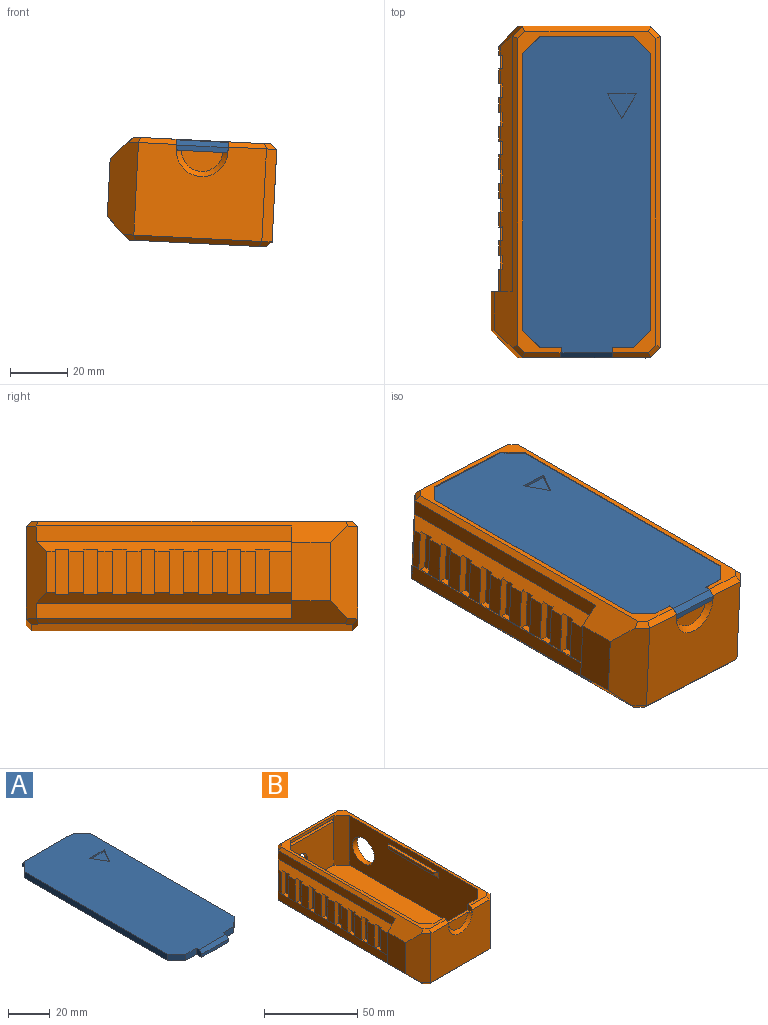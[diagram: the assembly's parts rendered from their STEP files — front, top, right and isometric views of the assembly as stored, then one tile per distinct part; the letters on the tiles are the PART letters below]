
ASSEMBLY  parts=2 mates=1
PART A: 24 faces, bbox 44.7x114.1x3.6 mm
  f0: plane 110.45x44.65mm, normal (0,0,1), area 4768.4mm2, adj f1,f2,f3,f4,f5,f7,f8,f9
  f1: plane 7.33x3.6mm, normal (0,-1,0), area 26.4mm2, adj f0,f6,f9,f16
  f2: plane 7.33x3.6mm, normal (0,-1,0), area 26.4mm2, adj f0,f6,f10,f17
  f3: plane 96.66x3.6mm, normal (1,0,0), area 348mm2, adj f0,f6,f7,f10
  f4: plane 32.65x1.8mm, normal (0,1,0), area 58.8mm2, adj f0,f7,f8,f11
  f5: plane 96.66x3.6mm, normal (-1,0,0), area 348mm2, adj f0,f6,f8,f9
  f6: plane 114.05x44.65mm, normal (0,0,-1), area 4902.9mm2, adj f1,f2,f3,f5,f7,f8,f9,f10
  f7: plane 6x6mm, normal (0.71,0.71,0), area 30.5mm2, adj f0,f3,f4,f6,f12
  f8: plane 6x6mm, normal (-0.71,0.71,0), area 30.5mm2, adj f0,f4,f5,f6,f13
  f9: plane 6x6mm, normal (-0.71,-0.71,0), area 30.5mm2, adj f0,f1,f5,f6
  f10: plane 6x6mm, normal (0.71,-0.71,0), area 30.5mm2, adj f0,f2,f3,f6
  f11: plane 32.65x1.55mm, normal (0,0,1), area 50.6mm2, adj f4,f12,f13,f15
  f12: plane 1.8x1.8mm, normal (1,0,0), area 3.2mm2, adj f6,f7,f11,f14,f15
  f13: plane 1.8x1.8mm, normal (-1,0,0), area 3.2mm2, adj f6,f8,f11,f14,f15
  f14: plane 32.65x1.55mm, normal (0,1,0), area 50.6mm2, adj f6,f12,f13,f15
  f15: cylinder r=0.25mm len=32.65mm, axis (-1,0,0), area 12.8mm2, adj f11,f12,f13,f14
  f16: plane 3.6x3.6mm, normal (-1,0,0), area 11.3mm2, adj f0,f1,f6,f18,f19
  f17: plane 3.6x3.6mm, normal (1,0,0), area 11.3mm2, adj f0,f2,f6,f18,f19
  f18: plane 18x1.8mm, normal (0,-1,0), area 32.4mm2, adj f6,f16,f17,f19
  f19: plane 18x1.8mm, normal (0,-0.71,0.71), area 45.8mm2, adj f0,f16,f17,f18
  f20: plane 8.66x5mm, normal (0.87,0.5,0), area 9mm2, adj f0,f21,f22,f23
  f21: plane 8.66x5mm, normal (-0.87,0.5,0), area 9mm2, adj f0,f20,f22,f23
  f22: plane 10x0.9mm, normal (0,-1,0), area 9mm2, adj f0,f20,f21,f23
  f23: plane 10x8.66mm, normal (0,0,1), area 43.3mm2, adj f20,f21,f22
PART B: 141 faces, bbox 58x116x36 mm
  f0: plane 14.4x3.01mm, normal (-1,0,0), area 43.4mm2, adj f21,f74,f75,f113
  f1: plane 14.4x5.23mm, normal (-1,0,0), area 75.3mm2, adj f74,f75,f109,f111
  f2: plane 14.4x5.23mm, normal (-1,0,0), area 75.3mm2, adj f74,f75,f104,f107
  f3: plane 14.4x5.23mm, normal (-1,0,0), area 75.3mm2, adj f74,f75,f99,f102
  f4: plane 14.4x5.23mm, normal (-1,0,0), area 75.3mm2, adj f74,f75,f94,f97
  f5: plane 14.4x5.23mm, normal (-1,0,0), area 75.3mm2, adj f74,f75,f89,f92
  f6: plane 14.4x5.23mm, normal (-1,0,0), area 75.3mm2, adj f74,f75,f84,f87
  f7: plane 14.4x5.23mm, normal (-1,0,0), area 75.3mm2, adj f74,f75,f79,f82
  f8: plane 89.2x5.4mm, normal (-1,0,0), area 481.7mm2, adj f21,f64,f72,f75
  f9: plane 89.2x5.4mm, normal (-1,0,0), area 481.7mm2, adj f21,f61,f72,f74
  f10: plane 96.81x32.4mm, normal (1,0,0), area 2998.7mm2, adj f14,f20,f26,f28,f44,f49,f50,f51
  f11: plane 96.81x32.4mm, normal (-1,0,0), area 2784.8mm2, adj f14,f20,f25,f27,f30,f42,f46,f47
  f12: plane 44.8x32.4mm, normal (0,1,0), area 999.1mm2, adj f21,f22,f39,f58,f66
  f13: plane 32.8x1.8mm, normal (0,-1,0), area 59mm2, adj f14,f27,f28,f37
  f14: plane 112.4x48.4mm, normal (0,0,1), area 592.5mm2, adj f10,f11,f13,f15,f25,f26,f27,f28
  f15: plane 32.8x32.4mm, normal (0,1,0), area 998.1mm2, adj f14,f20,f25,f26,f31,f32,f33
  f16: plane 44.8x32.4mm, normal (0,-1,0), area 1291.9mm2, adj f23,f24,f31,f33,f53,f57,f62,f70
  f17: plane 32.8x28.6mm, normal (0,-1,0), area 851.6mm2, adj f20,f27,f28,f29,f35
  f18: plane 108.8x32.4mm, normal (1,0,0), area 2646.8mm2, adj f22,f23,f30,f54,f68,f116,f117,f118
  f19: plane 112.4x48.4mm, normal (0,0,-1), area 5427.2mm2, adj f54,f55,f56,f57,f58,f59,f60,f61
  f20: plane 108.8x44.8mm, normal (0,0,1), area 4802.3mm2, adj f10,f11,f15,f17,f25,f26,f27,f28
  f21: plane 32.4x7.2mm, normal (-0.71,0.71,0), area 256.6mm2, adj f0,f8,f9,f12,f60,f65,f74,f75
  f22: plane 32.4x3.6mm, normal (0.71,0.71,0), area 165mm2, adj f12,f18,f56,f67
  f23: plane 32.4x3.6mm, normal (0.71,-0.71,0), area 165mm2, adj f16,f18,f55,f69
  f24: plane 32.4x9.6mm, normal (-0.71,-0.71,0), area 388.9mm2, adj f16,f59,f61,f63,f64,f73
  f25: plane 32.4x6mm, normal (-0.71,0.71,0), area 274.8mm2, adj f11,f14,f15,f20
  f26: plane 32.4x6mm, normal (0.71,0.71,0), area 274.8mm2, adj f10,f14,f15,f20
  f27: plane 32.4x6mm, normal (-0.71,-0.71,0), area 274.8mm2, adj f11,f13,f14,f17,f20,f36
  f28: plane 32.4x6mm, normal (0.71,-0.71,0), area 274.8mm2, adj f10,f13,f14,f17,f20,f34
  f29: cylinder r=5.25mm len=10.5mm, axis (0,1,0), area 85.8mm2, adj f17,f40
  f30: cylinder r=8.25mm len=16.5mm, axis (1,0,0), area 186.6mm2, adj f11,f18
  f31: plane 3.6x3.6mm, normal (1,0,0), area 11.3mm2, adj f14,f15,f16,f32,f62
  f32: plane 18x3.6mm, normal (0,0,1), area 35.6mm2, adj f15,f31,f33,f52,f53
  f33: plane 3.6x3.6mm, normal (-1,0,0), area 11.3mm2, adj f14,f15,f16,f32,f70
  f34: plane 2.1x2mm, normal (1,0,0), area 4.1mm2, adj f28,f35,f37,f38,f41
  f35: plane 32.8x2.1mm, normal (0,0,1), area 68.9mm2, adj f17,f34,f36,f38
  f36: plane 2.1x2mm, normal (-1,0,0), area 4.1mm2, adj f27,f35,f37,f38,f41
  f37: plane 32.8x1.6mm, normal (0,0,-1), area 52.5mm2, adj f13,f34,f36,f41
  f38: plane 32.8x1.5mm, normal (0,-1,0), area 49.2mm2, adj f34,f35,f36,f41
  f39: cylinder r=12mm len=24mm, axis (0,1,0), area 75.4mm2, adj f12,f40
  f40: plane 24x24mm, normal (0,1,0), area 365.8mm2, adj f29,f39
  f41: cylinder r=0.5mm len=32.8mm, axis (-1,0,0), area 25.8mm2, adj f34,f36,f37,f38
  f42: plane 38.28x1.8mm, normal (0,0,1), area 65.7mm2, adj f11,f43,f46,f48
  f43: plane 34.68x1.8mm, normal (-1,0,0), area 62.4mm2, adj f42,f46,f47,f48
  f44: plane 38.28x1.8mm, normal (0,0,1), area 65.7mm2, adj f10,f45,f49,f51
  f45: plane 34.68x1.8mm, normal (1,0,0), area 62.4mm2, adj f44,f49,f50,f51
  f46: plane 3.6x1.8mm, normal (-0.71,0.71,0), area 6.9mm2, adj f11,f42,f43,f47
  f47: plane 38.28x1.8mm, normal (-0.71,0,-0.71), area 92.9mm2, adj f11,f43,f46,f48
  f48: plane 3.6x1.8mm, normal (-0.71,-0.71,0), area 6.9mm2, adj f11,f42,f43,f47
  f49: plane 3.6x1.8mm, normal (0.71,-0.71,0), area 6.9mm2, adj f10,f44,f45,f50
  f50: plane 38.28x1.8mm, normal (0.71,0,-0.71), area 92.9mm2, adj f10,f45,f49,f51
  f51: plane 3.6x1.8mm, normal (0.71,0.71,0), area 6.9mm2, adj f10,f44,f45,f50
  f52: plane 14.4x7.2mm, normal (0,-1,0), area 81.4mm2, adj f32,f53
  f53: cone r=7.2mm half-angle=45deg, axis (0,-1,0), area 64.8mm2, adj f16,f32,f52
  f54: plane 108.8x1.8mm, normal (0.71,0,-0.71), area 275.1mm2, adj f18,f19,f55,f56
  f55: plane 4.35x4.35mm, normal (0.5,-0.5,-0.71), area 11.1mm2, adj f19,f23,f54,f57
  f56: plane 4.35x4.35mm, normal (0.5,0.5,-0.71), area 11.1mm2, adj f19,f22,f54,f58
  f57: plane 44.8x1.8mm, normal (0,-0.71,-0.71), area 112.1mm2, adj f16,f19,f55,f59
  f58: plane 44.8x1.8mm, normal (0,0.71,-0.71), area 112.1mm2, adj f12,f19,f56,f60
  f59: plane 4.35x4.35mm, normal (-0.5,-0.5,-0.71), area 11.1mm2, adj f19,f24,f57,f61
  f60: plane 4.35x4.35mm, normal (-0.5,0.5,-0.71), area 11.1mm2, adj f19,f21,f58,f61
  f61: plane 108.8x7.8mm, normal (-0.71,0,-0.71), area 415.9mm2, adj f9,f19,f24,f59,f60,f72,f73
  f62: plane 13.4x1.8mm, normal (0,-0.71,0.71), area 33.2mm2, adj f14,f16,f31,f63
  f63: plane 4.35x4.35mm, normal (-0.5,-0.5,0.71), area 11.1mm2, adj f14,f24,f62,f64
  f64: plane 108.8x7.8mm, normal (-0.71,0,0.71), area 415.9mm2, adj f8,f14,f24,f63,f65,f72,f73
  f65: plane 4.35x4.35mm, normal (-0.5,0.5,0.71), area 11.1mm2, adj f14,f21,f64,f66
  f66: plane 44.8x1.8mm, normal (0,0.71,0.71), area 112.1mm2, adj f12,f14,f65,f67
  f67: plane 4.35x4.35mm, normal (0.5,0.5,0.71), area 11.1mm2, adj f14,f22,f66,f68
  f68: plane 108.8x1.8mm, normal (0.71,0,0.71), area 275.1mm2, adj f14,f18,f67,f69
  f69: plane 4.35x4.35mm, normal (0.5,-0.5,0.71), area 11.1mm2, adj f14,f23,f68,f70
  f70: plane 13.4x1.8mm, normal (0,-0.71,0.71), area 33.2mm2, adj f14,f16,f33,f69
  f71: plane 14.4x7.78mm, normal (-1,0,0), area 112mm2, adj f72,f74,f75,f77
  f72: plane 32.4x6mm, normal (0,1,0), area 93.6mm2, adj f8,f9,f61,f64,f71,f73,f74,f75
  f73: plane 20.41x13.6mm, normal (-1,0,0), area 277.6mm2, adj f24,f61,f64,f72
  f74: plane 89.2x3.6mm, normal (-0.71,0,-0.71), area 410.6mm2, adj f0,f1,f2,f3,f4,f5,f6,f7
  f75: plane 89.2x3.6mm, normal (-0.71,0,0.71), area 410.6mm2, adj f0,f1,f2,f3,f4,f5,f6,f7
  f76: plane 4.78x2.36mm, normal (0,0,1), area 11.3mm2, adj f74,f77,f79,f80
  f77: plane 15.67x3mm, normal (0,1,0), area 46.6mm2, adj f71,f74,f75,f76,f78,f80
  f78: plane 4.78x2.36mm, normal (0,0,-1), area 11.3mm2, adj f75,f77,f79,f80
  f79: plane 15.67x3mm, normal (0,-1,0), area 46.6mm2, adj f7,f74,f75,f76,f78,f80
  f80: plane 15.67x4.78mm, normal (-1,0,0), area 74.8mm2, adj f76,f77,f78,f79
  f81: plane 4.78x2.36mm, normal (0,0,1), area 11.3mm2, adj f74,f82,f84,f85
  f82: plane 15.67x3mm, normal (0,1,0), area 46.6mm2, adj f7,f74,f75,f81,f83,f85
  f83: plane 4.78x2.36mm, normal (0,0,-1), area 11.3mm2, adj f75,f82,f84,f85
  f84: plane 15.67x3mm, normal (0,-1,0), area 46.6mm2, adj f6,f74,f75,f81,f83,f85
  f85: plane 15.67x4.78mm, normal (-1,0,0), area 74.8mm2, adj f81,f82,f83,f84
  f86: plane 4.78x2.36mm, normal (0,0,1), area 11.3mm2, adj f74,f87,f89,f90
  f87: plane 15.67x3mm, normal (0,1,0), area 46.6mm2, adj f6,f74,f75,f86,f88,f90
  f88: plane 4.78x2.36mm, normal (0,0,-1), area 11.3mm2, adj f75,f87,f89,f90
  f89: plane 15.67x3mm, normal (0,-1,0), area 46.6mm2, adj f5,f74,f75,f86,f88,f90
  f90: plane 15.67x4.78mm, normal (-1,0,0), area 74.8mm2, adj f86,f87,f88,f89
  f91: plane 4.78x2.36mm, normal (0,0,1), area 11.3mm2, adj f74,f92,f94,f95
  f92: plane 15.67x3mm, normal (0,1,0), area 46.6mm2, adj f5,f74,f75,f91,f93,f95
  f93: plane 4.78x2.36mm, normal (0,0,-1), area 11.3mm2, adj f75,f92,f94,f95
  f94: plane 15.67x3mm, normal (0,-1,0), area 46.6mm2, adj f4,f74,f75,f91,f93,f95
  f95: plane 15.67x4.78mm, normal (-1,0,0), area 74.8mm2, adj f91,f92,f93,f94
  f96: plane 4.78x2.36mm, normal (0,0,1), area 11.3mm2, adj f74,f97,f99,f100
  f97: plane 15.67x3mm, normal (0,1,0), area 46.6mm2, adj f4,f74,f75,f96,f98,f100
  f98: plane 4.78x2.36mm, normal (0,0,-1), area 11.3mm2, adj f75,f97,f99,f100
  f99: plane 15.67x3mm, normal (0,-1,0), area 46.6mm2, adj f3,f74,f75,f96,f98,f100
  f100: plane 15.67x4.78mm, normal (-1,0,0), area 74.8mm2, adj f96,f97,f98,f99
  f101: plane 4.78x2.36mm, normal (0,0,1), area 11.3mm2, adj f74,f102,f104,f105
  f102: plane 15.67x3mm, normal (0,1,0), area 46.6mm2, adj f3,f74,f75,f101,f103,f105
  f103: plane 4.78x2.36mm, normal (0,0,-1), area 11.3mm2, adj f75,f102,f104,f105
  f104: plane 15.67x3mm, normal (0,-1,0), area 46.6mm2, adj f2,f74,f75,f101,f103,f105
  f105: plane 15.67x4.78mm, normal (-1,0,0), area 74.8mm2, adj f101,f102,f103,f104
  f106: plane 4.78x2.36mm, normal (0,0,1), area 11.3mm2, adj f74,f107,f109,f110
  f107: plane 15.67x3mm, normal (0,1,0), area 46.6mm2, adj f2,f74,f75,f106,f108,f110
  f108: plane 4.78x2.36mm, normal (0,0,-1), area 11.3mm2, adj f75,f107,f109,f110
  f109: plane 15.67x3mm, normal (0,-1,0), area 46.6mm2, adj f1,f74,f75,f106,f108,f110
  f110: plane 15.67x4.78mm, normal (-1,0,0), area 74.8mm2, adj f106,f107,f108,f109
  f111: plane 15.67x3mm, normal (0,1,0), area 46.6mm2, adj f1,f74,f75,f112,f114,f115
  f112: plane 4.78x2.36mm, normal (0,0,-1), area 11.3mm2, adj f75,f111,f113,f115
  f113: plane 15.67x3mm, normal (0,-1,0), area 46.6mm2, adj f0,f74,f75,f112,f114,f115
  f114: plane 4.78x2.36mm, normal (0,0,1), area 11.3mm2, adj f74,f111,f113,f115
  f115: plane 15.67x4.78mm, normal (-1,0,0), area 74.8mm2, adj f111,f112,f113,f114
  f116: plane 25.4x5.23mm, normal (0,-0.98,0.2), area 23.3mm2, adj f18,f117,f119,f120
  f117: plane 5.23x0.9mm, normal (0,0,-1), area 4.7mm2, adj f18,f116,f118,f120
  f118: plane 25.4x5.23mm, normal (0,0.98,-0.2), area 23.3mm2, adj f18,f117,f119,f120
  f119: plane 5.23x0.9mm, normal (0,0,1), area 4.7mm2, adj f18,f116,f118,f120
  f120: plane 25.4x10.47mm, normal (1,0,0), area 132.9mm2, adj f116,f117,f118,f119
  f121: plane 25.4x5.23mm, normal (0,0.98,-0.2), area 23.3mm2, adj f18,f122,f124,f125
  f122: plane 5.23x0.9mm, normal (0,0,1), area 4.7mm2, adj f18,f121,f123,f125
  f123: plane 25.4x5.23mm, normal (0,-0.98,0.2), area 23.3mm2, adj f18,f122,f124,f125
  f124: plane 5.23x0.9mm, normal (0,0,-1), area 4.7mm2, adj f18,f121,f123,f125
  f125: plane 25.4x10.47mm, normal (1,0,0), area 132.9mm2, adj f121,f122,f123,f124
  f126: plane 25.4x5.23mm, normal (0,0.98,-0.2), area 23.3mm2, adj f18,f127,f129,f130
  f127: plane 5.23x0.9mm, normal (0,0,1), area 4.7mm2, adj f18,f126,f128,f130
  f128: plane 25.4x5.23mm, normal (0,-0.98,0.2), area 23.3mm2, adj f18,f127,f129,f130
  f129: plane 5.23x0.9mm, normal (0,0,-1), area 4.7mm2, adj f18,f126,f128,f130
  f130: plane 25.4x10.47mm, normal (1,0,0), area 132.9mm2, adj f126,f127,f128,f129
  f131: plane 25.4x5.23mm, normal (0,0.98,-0.2), area 23.3mm2, adj f18,f132,f134,f135
  f132: plane 5.23x0.9mm, normal (0,0,1), area 4.7mm2, adj f18,f131,f133,f135
  f133: plane 25.4x5.23mm, normal (0,-0.98,0.2), area 23.3mm2, adj f18,f132,f134,f135
  f134: plane 5.23x0.9mm, normal (0,0,-1), area 4.7mm2, adj f18,f131,f133,f135
  f135: plane 25.4x10.47mm, normal (1,0,0), area 132.9mm2, adj f131,f132,f133,f134
  f136: plane 25.4x5.23mm, normal (0,0.98,-0.2), area 23.3mm2, adj f18,f137,f139,f140
  f137: plane 5.23x0.9mm, normal (0,0,1), area 4.7mm2, adj f18,f136,f138,f140
  f138: plane 25.4x5.23mm, normal (0,-0.98,0.2), area 23.3mm2, adj f18,f137,f139,f140
  f139: plane 5.23x0.9mm, normal (0,0,-1), area 4.7mm2, adj f18,f136,f138,f140
  f140: plane 25.4x10.47mm, normal (1,0,0), area 132.9mm2, adj f136,f137,f138,f139
PLACE A rot(axis=(0,1,0),2.9deg) t=(42.41,-35.79,41.15)mm
PLACE B rot(axis=(0,1,0),2.9deg) t=(40.8,-35.77,8.99)mm
MATE fastened B.f35 <-> A.f6  axis (0.05,0,1) through (42.41,20.73,41.15)mm
